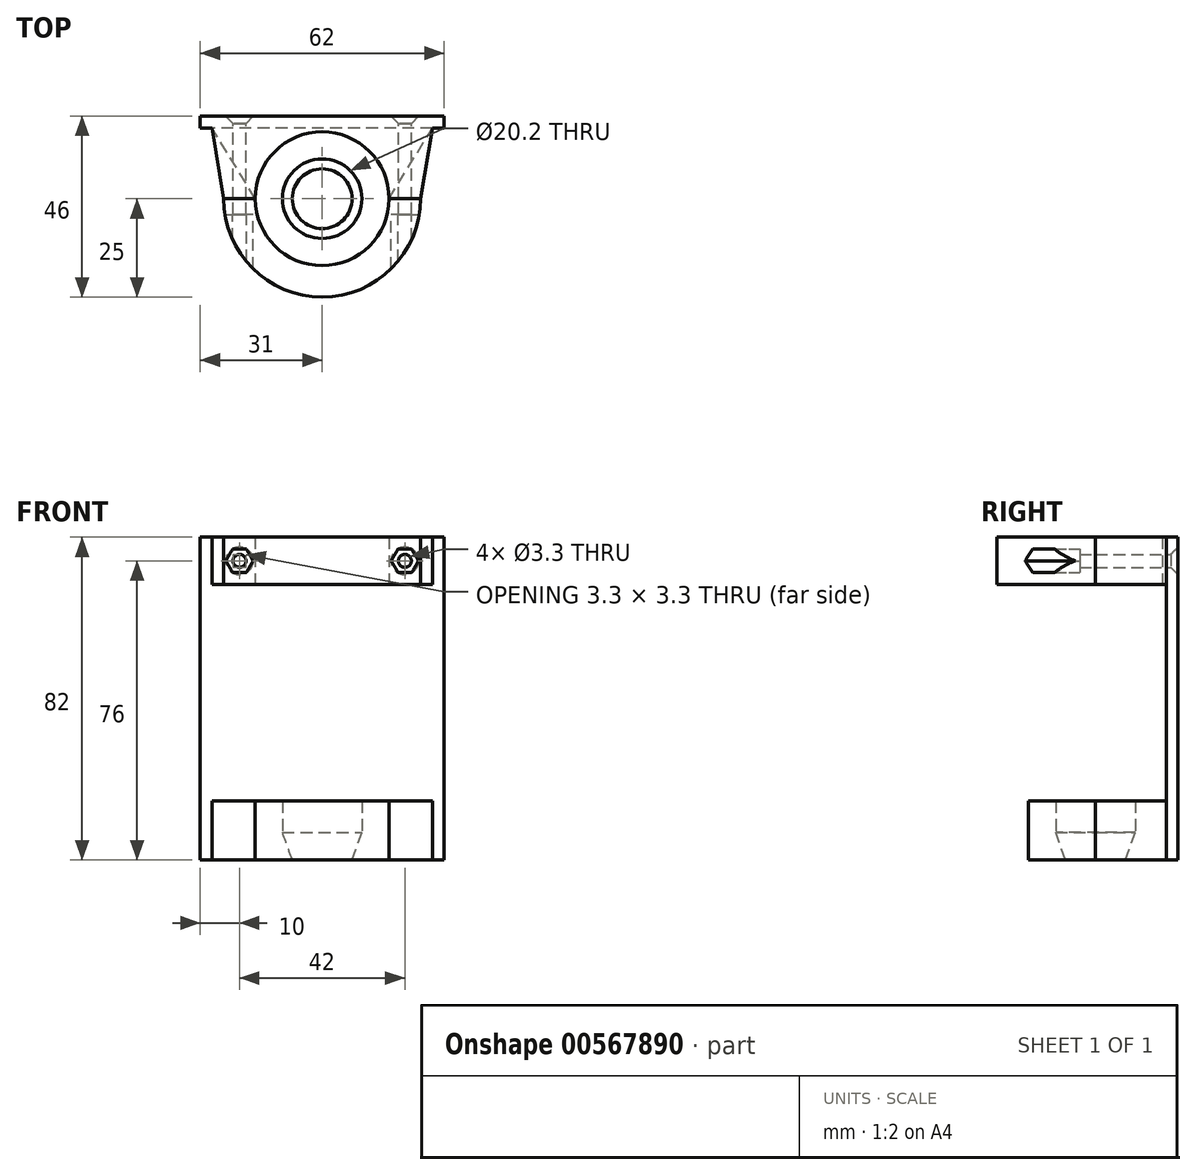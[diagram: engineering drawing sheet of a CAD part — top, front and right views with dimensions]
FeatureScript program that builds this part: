
annotation { "Feature Type Name" : "Feature", "Feature Type Description" : "" }
export const myFeature = defineFeature(function(context is Context, id is Id, definition is map)
    precondition{}
    {
        {
            var Q0;
            Q0=qCreatedBy(makeId("Top.planeOp"),FACE);
            var sketch = newSketch(context, id + "F0", { "sketchPlane" : qUnion([Q0])});
            skLineSegment(sketch, "E0.bottom", {"start": v(31, -1.5) * mm, "end": v(-31, -1.5) * mm});
            skLineSegment(sketch, "E0.top", {"start": v(31, 1.5) * mm, "end": v(-31, 1.5) * mm});
            skLineSegment(sketch, "E0.left", {"start": v(31, -1.5) * mm, "end": v(31, 1.5) * mm});
            skLineSegment(sketch, "E0.right", {"start": v(-31, -1.5) * mm, "end": v(-31, 1.5) * mm});
            skPoint(sketch, "E0.middle", {"position": v(0, 0) * mm});
            skCircle(sketch, "E1", {"center": v(0, -19.5) * mm, "radius": 7.6 * mm});
            skLineSegment(sketch, "E2", {"start": v(0, 1.5) * mm, "end": v(0, -19.5) * mm, "construction": true});
            skCircle(sketch, "E3", {"center": v(0, -19.5) * mm, "radius": 17 * mm});
            skLineSegment(sketch, "E4", {"start": v(-17, -19.5) * mm, "end": v(-25, -19.5) * mm});
            skLineSegment(sketch, "E5", {"start": v(-25, -19.5) * mm, "end": v(-28, -1.5) * mm});
            skLineSegment(sketch, "E6.MirrorCS", {"start": v(25, -19.5) * mm, "end": v(28, -1.5) * mm});
            skLineSegment(sketch, "E7.MirrorCS", {"start": v(17, -19.5) * mm, "end": v(25, -19.5) * mm});
            skArc(sketch, "E8", {"start": v(-25, -19.5) * mm, "mid": v(0, -44.5) * mm, "end": v(25, -19.5) * mm});
            skCircle(sketch, "E9", {"center": v(0, -19.5) * mm, "radius": 10.1 * mm});
            skLineSegment(sketch, "E10", {"start": v(17, -19.5) * mm, "end": v(28, -1.5) * mm});
            skLineSegment(sketch, "E11", {"start": v(-17, -19.5) * mm, "end": v(-28, -1.5) * mm});
            skSolve(sketch);
        }
        {
            var Q0;
            Q0=makeQuery(id+"F0.imprint","IMPRINT",FACE,{"disambiguationData":[TD([[makeQuery(id+"F0.imprint","IMPRINT",EDGE,{"derivedFrom":sQuery(id+"F0.wireOp",EDGE,"E0.top")}),1.0]])]});
            extrude(context, id + "F1", {"entities" : qUnion([Q0]), "depth" : 82 * mm, "offsetDistance" : 25 * mm});
        }
        {
            var Q0;
            {var subQ2=sQuery(id+"F0.wireOp",EDGE,"E10");Q0=makeQuery(id+"F0.imprint","IMPRINT",FACE,{"disambiguationData":[TD([[makeQuery(id+"F0.imprint","IMPRINT",EDGE,{"derivedFrom":subQ2}),1.0]])]});}
            var Q1;
            Q1=makeQuery(id+"F0.imprint","IMPRINT",FACE,{"disambiguationData":[TD([[makeQuery(id+"F0.imprint","IMPRINT",EDGE,{"derivedFrom":sQuery(id+"F0.wireOp",EDGE,"E6.MirrorCS")}),1.0]])]});
            var Q2;
            Q2=makeQuery(id+"F0.imprint","IMPRINT",FACE,{"disambiguationData":[TD([[makeQuery(id+"F0.imprint","IMPRINT",EDGE,{"derivedFrom":sQuery(id+"F0.wireOp",EDGE,"E4")}),-1.0]])]});
            extrude(context, id + "F2", {"entities" : qUnion([Q0, Q1, Q2]), "operationType" : NewBodyOperationType.ADD, "depth" : 82 * mm, "offsetDistance" : 25 * mm, "hasSecondDirection" : true, "secondDirectionOppositeDirection" : false, "secondDirectionDepth" : 70 * mm});
        }
        {
            var Q0;
            {var subQ0=sQuery(id+"F0.wireOp",EDGE,"E4");Q0=makeQuery(id+"F0.imprint","IMPRINT",FACE,{"disambiguationData":[TD([[makeQuery(id+"F0.imprint","IMPRINT",EDGE,{"derivedFrom":subQ0}),1.0]])]});}
            extrude(context, id + "F3", {"entities" : qUnion([Q0]), "depth" : 82 * mm, "offsetDistance" : 25 * mm, "hasSecondDirection" : true, "secondDirectionOppositeDirection" : false, "secondDirectionDepth" : 70 * mm});
        }
        {
            var Q0;
            Q0=makeQuery(id+"F1.opExtrude","SWEPT_FACE",FACE,{"disambiguationData":[OSD([sQuery(id+"F0.wireOp",EDGE,"E0.top")])]});
            var sketch = newSketch(context, id + "F4", { "sketchPlane" : qUnion([Q0])});
            skPoint(sketch, "E12", {"position": v(21, 76) * mm});
            skLineSegment(sketch, "E13", {"start": v(0, 82.24) * mm, "end": v(0, 61.73) * mm, "construction": true});
            skPoint(sketch, "E14.MirrorP", {"position": v(-21, 76) * mm});
            skCircle(sketch, "E15", {"center": v(-21, 76) * mm, "radius": 3 * mm, "construction": true});
            skLineSegment(sketch, "E16", {"start": v(-24.46, 76) * mm, "end": v(-17.54, 76) * mm, "construction": true});
            skLineSegment(sketch, "E17", {"start": v(-22.73, 79) * mm, "end": v(-19.27, 73) * mm, "construction": true});
            skLineSegment(sketch, "E18", {"start": v(-19.27, 79) * mm, "end": v(-22.73, 73) * mm, "construction": true});
            skLineSegment(sketch, "E19", {"start": v(-21, 79) * mm, "end": v(-22.73, 79) * mm});
            skLineSegment(sketch, "E20", {"start": v(-22.73, 79) * mm, "end": v(-24.46, 76) * mm});
            skLineSegment(sketch, "E21", {"start": v(-24.46, 76) * mm, "end": v(-22.73, 73) * mm});
            skLineSegment(sketch, "E22", {"start": v(-22.73, 73) * mm, "end": v(-19.27, 73) * mm});
            skLineSegment(sketch, "E23", {"start": v(-19.27, 73) * mm, "end": v(-17.54, 76) * mm});
            skLineSegment(sketch, "E24", {"start": v(-17.54, 76) * mm, "end": v(-19.27, 79) * mm});
            skLineSegment(sketch, "E25", {"start": v(-19.27, 79) * mm, "end": v(-21, 79) * mm});
            skLineSegment(sketch, "E26.MirrorCS", {"start": v(17.54, 76) * mm, "end": v(19.27, 79) * mm});
            skLineSegment(sketch, "E27.MirrorCS", {"start": v(19.27, 73) * mm, "end": v(17.54, 76) * mm});
            skLineSegment(sketch, "E28.MirrorCS", {"start": v(22.73, 73) * mm, "end": v(19.27, 73) * mm});
            skLineSegment(sketch, "E29.MirrorCS", {"start": v(24.46, 76) * mm, "end": v(22.73, 73) * mm});
            skLineSegment(sketch, "E30.MirrorCS", {"start": v(22.73, 79) * mm, "end": v(24.46, 76) * mm});
            skLineSegment(sketch, "E31.MirrorCS", {"start": v(21, 79) * mm, "end": v(22.73, 79) * mm});
            skLineSegment(sketch, "E32.MirrorCS", {"start": v(19.27, 79) * mm, "end": v(21, 79) * mm});
            skSolve(sketch);
        }
        {
            var Q0;
            Q0=sQuery(id+"F4.wireOp",VERTEX,"E14.MirrorP");
            var Q1;
            Q1=sQuery(id+"F4.wireOp",VERTEX,"E12");
            var Q2;
            Q2=makeQuery(id+"F1.opExtrude","SWEPT_BODY",BODY,{"disambiguationData":[OSD([sQuery(id+"F0.wireOp",EDGE,"E0.top"),sQuery(id+"F0.wireOp",EDGE,"E0.left"),sQuery(id+"F0.wireOp",EDGE,"E0.right"),sQuery(id+"F0.wireOp",EDGE,"W0TwIUQh-f6X8-0WCO-OMY6-XX3QrrhDxWBs.bottom")])]});
            var Q3;
            Q3=makeQuery(id+"F3.opExtrude","SWEPT_BODY",BODY,{"disambiguationData":[OSD([sQuery(id+"F0.wireOp",EDGE,"E3"),sQuery(id+"F0.wireOp",EDGE,"E4"),sQuery(id+"F0.wireOp",EDGE,"E7.MirrorCS"),sQuery(id+"F0.wireOp",EDGE,"E8")])]});
            hole(context, id + "F5", {"style" : HoleStyle.C_SINK, "endStyle" : HoleEndStyle.THROUGH, "holeDiameter" : 3.3 * mm, "cSinkDiameter" : 7 * mm, "cSinkAngle" : 90 * degree, "majorDiameter" : 5 * mm, "isTappedThrough" : true, "tappedDepth" : 12 * mm, "tapClearance" : 3, "locations" : qUnion([Q0, Q1]), "scope" : qUnion([Q2, Q3])});
        }
        {
            var Q0;
            Q0=makeQuery(id+"F4.imprint","IMPRINT",FACE,{"disambiguationData":[TD([[makeQuery(id+"F4.imprint","IMPRINT",EDGE,{"derivedFrom":sQuery(id+"F4.wireOp",EDGE,"E19")}),1.0]])]});
            var Q1;
            Q1=makeQuery(id+"F4.imprint","IMPRINT",FACE,{"disambiguationData":[TD([[makeQuery(id+"F4.imprint","IMPRINT",EDGE,{"derivedFrom":sQuery(id+"F4.wireOp",EDGE,"E26.MirrorCS")}),-1.0]])]});
            extrude(context, id + "F6", {"entities" : qUnion([Q0, Q1]), "operationType" : NewBodyOperationType.REMOVE, "oppositeDirection" : true, "depth" : 50 * mm, "offsetDistance" : 25 * mm, "hasSecondDirection" : true, "secondDirectionOppositeDirection" : true, "secondDirectionDepth" : 25 * mm});
        }
        {
            var Q0;
            Q0=makeQuery(id+"F1.opExtrude","SWEPT_FACE",FACE,{"disambiguationData":[OSD([sQuery(id+"F0.wireOp",EDGE,"E0.bottom")])]});
            cPlane(context, id + "F7", {"entities" : qUnion([Q0]), "cplaneType" : CPlaneType.OFFSET, "offset" : 18 * mm, "width" : 150 * mm, "height" : 150 * mm});
        }
        {
            var Q0;
            Q0=makeQuery(id+"F0.imprint","IMPRINT",FACE,{"disambiguationData":[TD([[makeQuery(id+"F0.imprint","IMPRINT",EDGE,{"derivedFrom":sQuery(id+"F0.wireOp",EDGE,"E9")}),-1.0]])]});
            var Q1;
            {var subQ2=sQuery(id+"F0.wireOp",EDGE,"E10");Q1=makeQuery(id+"F0.imprint","IMPRINT",FACE,{"disambiguationData":[TD([[makeQuery(id+"F0.imprint","IMPRINT",EDGE,{"derivedFrom":subQ2}),1.0]])]});}
            extrude(context, id + "F8", {"entities" : qUnion([Q0, Q1]), "operationType" : NewBodyOperationType.ADD, "depth" : 15 * mm, "offsetDistance" : 25 * mm});
        }
        {
            var Q0;
            Q0=qCreatedBy(id+"F7.planeOp",FACE);
            var sketch = newSketch(context, id + "F9", { "sketchPlane" : qUnion([Q0])});
            skLineSegment(sketch, "E33", {"start": v(7.6, 0) * mm, "end": v(10.1, 7) * mm});
            skLineSegment(sketch, "E34", {"start": v(10.1, 7) * mm, "end": v(10.1, 0) * mm});
            skLineSegment(sketch, "E35", {"start": v(10.1, 0) * mm, "end": v(7.6, 0) * mm});
            skLineSegment(sketch, "E36", {"start": v(0, 0) * mm, "end": v(0, 7) * mm, "construction": true});
            skSolve(sketch);
        }
        {
            var Q0;
            Q0=makeQuery(id+"F9.imprint","IMPRINT",FACE,{"disambiguationData":[TD([[makeQuery(id+"F9.imprint","IMPRINT",EDGE,{"derivedFrom":sQuery(id+"F9.wireOp",EDGE,"E33")}),-1.0]])]});
            var Q1;
            Q1=sQuery(id+"F9.wireOp",EDGE,"E36");
            revolve(context, id + "F10", {"operationType" : NewBodyOperationType.ADD, "entities" : qUnion([Q0]), "axis" : qUnion([Q1]), "revolveType" : RevolveType.FULL});
        }
    });
